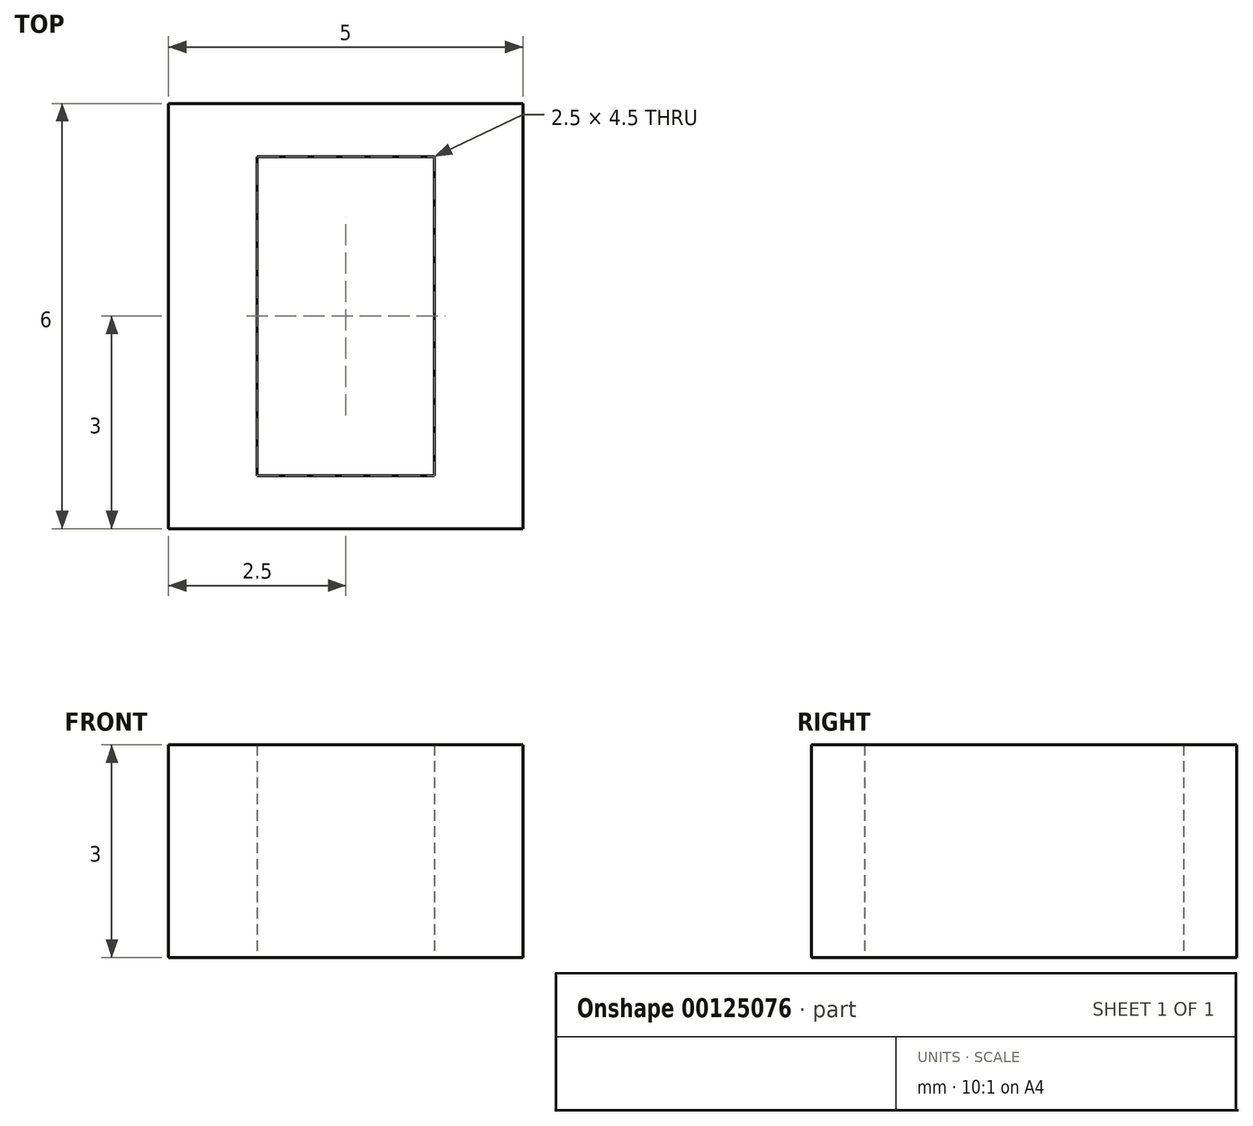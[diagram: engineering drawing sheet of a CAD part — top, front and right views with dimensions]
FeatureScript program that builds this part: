
annotation { "Feature Type Name" : "Feature", "Feature Type Description" : "" }
export const myFeature = defineFeature(function(context is Context, id is Id, definition is map)
    precondition{}
    {
        {
            var Q0;
            Q0=qCreatedBy(makeId("Top.planeOp"),FACE);
            var sketch = newSketch(context, id + "F0", { "sketchPlane" : qUnion([Q0])});
            skLineSegment(sketch, "E0.bottom", {"start": v(-1.25, 2.25) * mm, "end": v(1.25, 2.25) * mm});
            skLineSegment(sketch, "E0.top", {"start": v(-1.25, -2.25) * mm, "end": v(1.25, -2.25) * mm});
            skLineSegment(sketch, "E0.left", {"start": v(-1.25, 2.25) * mm, "end": v(-1.25, -2.25) * mm});
            skLineSegment(sketch, "E0.right", {"start": v(1.25, 2.25) * mm, "end": v(1.25, -2.25) * mm});
            skPoint(sketch, "E0.middle", {"position": v(0, 0) * mm});
            skLineSegment(sketch, "E1.bottom", {"start": v(-2.5, 3) * mm, "end": v(2.5, 3) * mm});
            skLineSegment(sketch, "E1.top", {"start": v(-2.5, -3) * mm, "end": v(2.5, -3) * mm});
            skLineSegment(sketch, "E1.left", {"start": v(-2.5, 3) * mm, "end": v(-2.5, -3) * mm});
            skLineSegment(sketch, "E1.right", {"start": v(2.5, 3) * mm, "end": v(2.5, -3) * mm});
            skSolve(sketch);
        }
        {
            var Q0;
            Q0 = qSketchRegion(id + "F0", true);
            var Q1;
            Q1=makeQuery(id+"F0.imprint","IMPRINT",FACE,{"disambiguationData":[TD([[makeQuery(id+"F0.imprint","IMPRINT",EDGE,{"derivedFrom":sQuery(id+"F0.wireOp",EDGE,"E0.bottom")}),1.0]])]});
            extrude(context, id + "F1", {"entities" : qUnion([Q0, Q1]), "depth" : 3 * mm});
        }
    });
